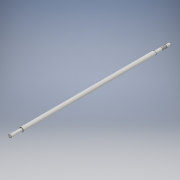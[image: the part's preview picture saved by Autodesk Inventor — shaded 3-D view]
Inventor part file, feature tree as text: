
AUTODESK INVENTOR PART (.ipt)
format: ipt  version: 2018 (Build 220112000, 112)  size: 109,568 bytes
history: native  units: mm
features: extrude x4, sketch x4, thread x1
ambient origin geometry x8: Origin, YZ Plane, XZ Plane, XY Plane, X Axis, Y Axis, Z Axis, Center Point
bodies: Solid1 (feature_tree)
feature tree (9):
  extrude  "Extrusion1"  Depth=464.0mm TaperAngle=0.0deg
  extrude  "Extrusion2"  Depth=40.0mm TaperAngle=0.0deg
  extrude  "Extrusion3"  Depth=15.0mm TaperAngle=0.0deg
  thread  "Thread1"  [1 undecoded]
  extrude  "Extrusion4"  Depth=40.0mm TaperAngle=0.0deg
  sketch  "Sketch1"  dims[d0=14.0mm d1=464.0mm d2=0.0mm]
  sketch  "Sketch2"  dims[d3=10.0mm d4=40.0mm d5=0.0mm]
  sketch  "Sketch3"  dims[d6=8.0mm d7=15.0mm d8=0.0mm d9=17.0mm d10=0.0mm]
  sketch  "Sketch4"  dims[d13=10.0mm d14=40.0mm d15=0.0mm]
note: 1 required parameter value undecoded (feature->parameter linkage not recoverable at this tier; creation-order binding heuristic only, values carry confidence <= 0.55)
